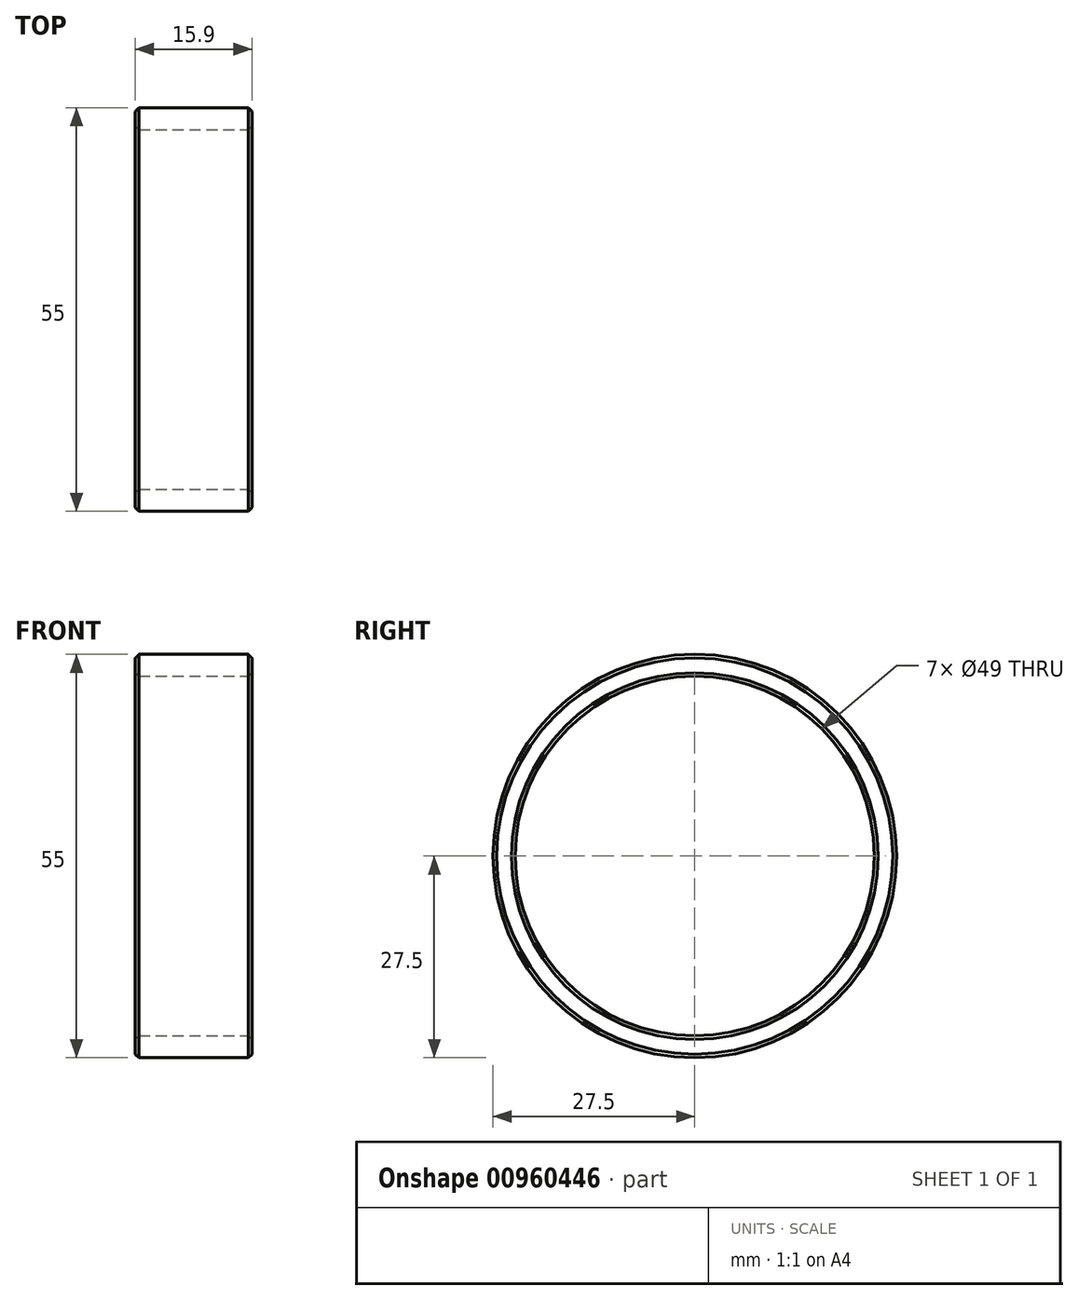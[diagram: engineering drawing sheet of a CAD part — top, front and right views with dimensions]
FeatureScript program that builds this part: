
annotation { "Feature Type Name" : "Feature", "Feature Type Description" : "" }
export const myFeature = defineFeature(function(context is Context, id is Id, definition is map)
    precondition{}
    {
        {
            var Q0;
            Q0=qCreatedBy(makeId("Front.planeOp"),FACE);
            var sketch = newSketch(context, id + "F0", { "sketchPlane" : qUnion([Q0])});
            skLineSegment(sketch, "E0.bottom", {"start": v(-20.39, 27.5) * mm, "end": v(-4.49, 27.5) * mm});
            skLineSegment(sketch, "E0.top", {"start": v(-20.39, 24.5) * mm, "end": v(-4.49, 24.5) * mm});
            skLineSegment(sketch, "E0.left", {"start": v(-20.39, 27.5) * mm, "end": v(-20.39, 24.5) * mm});
            skLineSegment(sketch, "E0.right", {"start": v(-4.49, 27.5) * mm, "end": v(-4.49, 24.5) * mm});
            skLineSegment(sketch, "E1", {"start": v(0, 0) * mm, "end": v(-25.15, 0) * mm});
            skSolve(sketch);
        }
        {
            var Q0;
            Q0 = qSketchRegion(id + "F0", true);
            var Q1;
            Q1=sQuery(id+"F0.wireOp",EDGE,"E1");
            revolve(context, id + "F1", {"surfaceOperationType" : NewSurfaceOperationType.NEW, "entities" : qUnion([Q0]), "axis" : qUnion([Q1]), "revolveType" : RevolveType.FULL});
        }
        {
            var Q0;
            Q0=makeQuery(id+"F1.opRevolve","SWEPT_FACE",FACE,{"disambiguationData":[OSD([sQuery(id+"F0.wireOp",EDGE,"E0.top")])]});
            var Q1;
            Q1=makeQuery(id+"F1.opRevolve","SWEPT_FACE",FACE,{"disambiguationData":[OSD([sQuery(id+"F0.wireOp",EDGE,"E0.bottom")])]});
            chamfer(context, id + "F2", {"entities" : qUnion([Q0, Q1]), "width" : 0.5 * mm, "tangentPropagation" : true});
        }
    });
